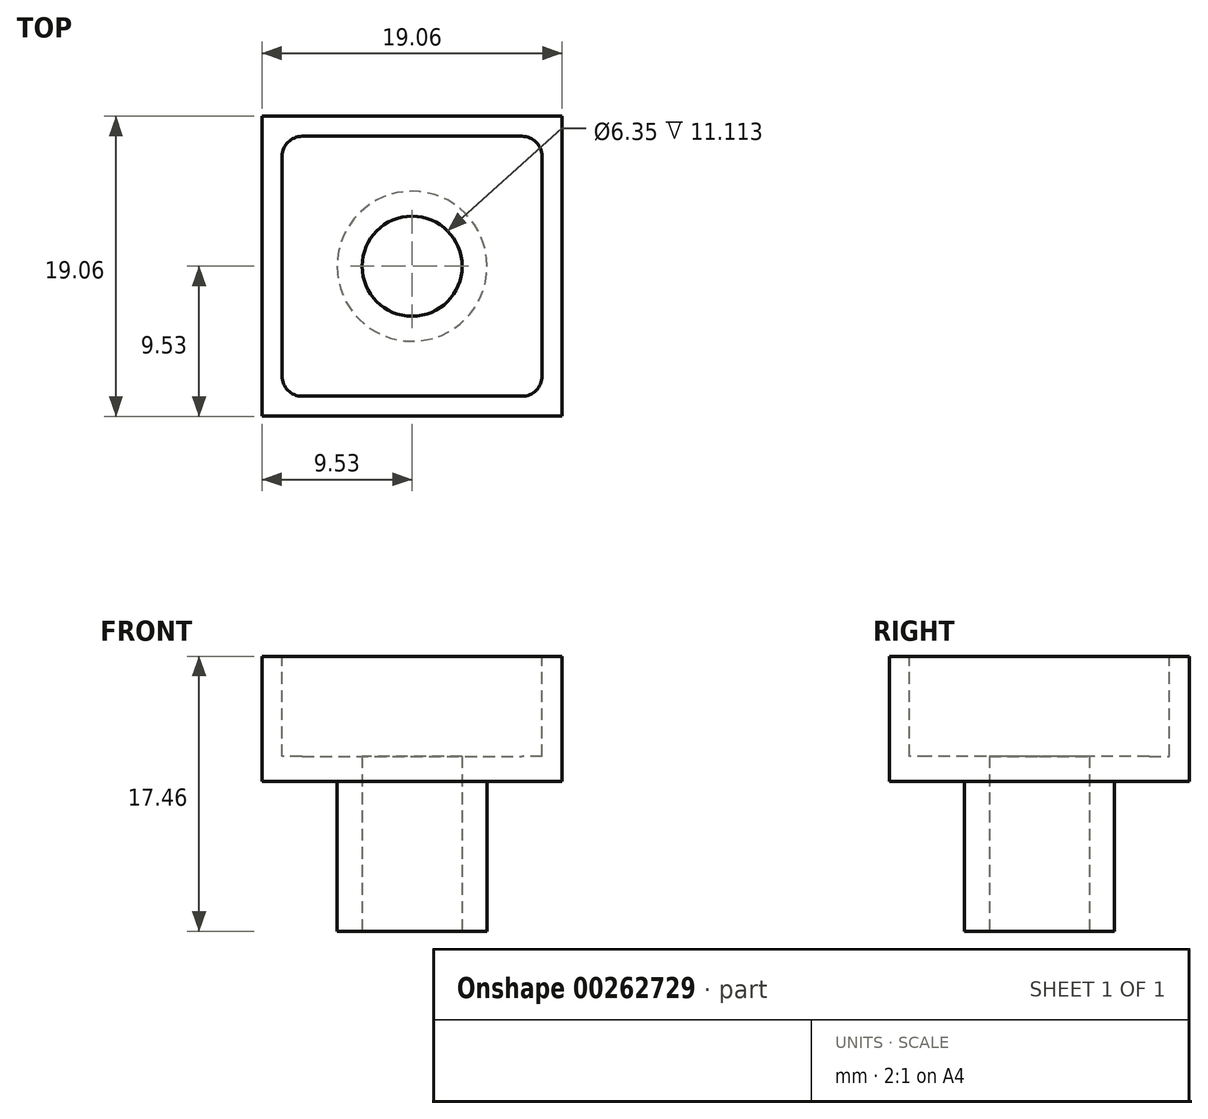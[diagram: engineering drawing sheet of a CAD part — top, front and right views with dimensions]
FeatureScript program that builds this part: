
annotation { "Feature Type Name" : "Feature", "Feature Type Description" : "" }
export const myFeature = defineFeature(function(context is Context, id is Id, definition is map)
    precondition{}
    {
        {
            var Q0;
            Q0=qCreatedBy(makeId("Top.planeOp"),FACE);
            var sketch = newSketch(context, id + "F0", { "sketchPlane" : qUnion([Q0])});
            skCircle(sketch, "E0", {"center": v(0, 0) * mm, "radius": 4.76 * mm});
            skSolve(sketch);
        }
        {
            var Q0;
            Q0 = qSketchRegion(id + "F0", true);
            extrude(context, id + "F1", {"entities" : qUnion([Q0]), "depth" : 17.46 * mm});
        }
        {
            var Q0;
            Q0=makeQuery(id+"F0.imprint","IMPRINT",FACE,{"disambiguationData":[TD([[makeQuery(id+"F0.imprint","IMPRINT",EDGE,{"derivedFrom":sQuery(id+"F0.wireOp",EDGE,"E0")}),1.0]])]});
            var sketch = newSketch(context, id + "F2", { "sketchPlane" : qUnion([Q0])});
            skCircle(sketch, "E1", {"center": v(0, 0) * mm, "radius": 3.18 * mm});
            skSolve(sketch);
        }
        {
            var Q0;
            Q0=qCreatedBy(makeId("Front.planeOp"),FACE);
            var sketch = newSketch(context, id + "F3", { "sketchPlane" : qUnion([Q0])});
            skLineSegment(sketch, "E2", {"start": v(0, 0) * mm, "end": v(0, 17.46) * mm, "construction": true});
            skLineSegment(sketch, "E3", {"start": v(0, 0) * mm, "end": v(-9.53, 0) * mm, "construction": true});
            skLineSegment(sketch, "E4.bottom", {"start": v(-9.52, 17.46) * mm, "end": v(9.52, 17.46) * mm});
            skLineSegment(sketch, "E4.top", {"start": v(-9.53, 9.53) * mm, "end": v(9.52, 9.53) * mm});
            skLineSegment(sketch, "E4.left", {"start": v(-9.53, 17.46) * mm, "end": v(-9.53, 9.53) * mm});
            skLineSegment(sketch, "E4.right", {"start": v(9.52, 17.46) * mm, "end": v(9.52, 9.53) * mm});
            skSolve(sketch);
        }
        {
            var Q0;
            Q0 = qSketchRegion(id + "F3", true);
            extrude(context, id + "F4", {"entities" : qUnion([Q0]), "operationType" : NewBodyOperationType.ADD, "endBound" : BoundingType.SYMMETRIC, "depth" : 19.05 * mm});
        }
        {
            var Q0;
            Q0=makeQuery(id+"F4.boolean.opBoolean","MERGE",FACE,{"derivedFrom":[makeQuery(id+"F1.opExtrude","CAP_FACE",FACE,{"disambiguationData":[OSD([sQuery(id+"F0.wireOp",EDGE,"E0")])],"isStart":false}),makeQuery(id+"F4.opExtrude","SWEPT_FACE",FACE,{"disambiguationData":[OSD([sQuery(id+"F3.wireOp",EDGE,"E4.bottom")])]})]});
            var sketch = newSketch(context, id + "F5", { "sketchPlane" : qUnion([Q0])});
            skLineSegment(sketch, "E5.bottom", {"start": v(-6.98, 8.26) * mm, "end": v(6.99, 8.26) * mm});
            skLineSegment(sketch, "E5.top", {"start": v(-6.98, -8.26) * mm, "end": v(6.99, -8.26) * mm});
            skLineSegment(sketch, "E5.left", {"start": v(-8.25, 6.99) * mm, "end": v(-8.25, -6.99) * mm});
            skLineSegment(sketch, "E5.right", {"start": v(8.26, 6.99) * mm, "end": v(8.26, -6.99) * mm});
            skPoint(sketch, "E6.visualSharp", {"position": v(-8.25, 8.26) * mm});
            skArc(sketch, "E6.filletArc", {"start": v(-6.98, 8.26) * mm, "mid": v(-7.88, 7.88) * mm, "end": v(-8.25, 6.99) * mm});
            skPoint(sketch, "E7.visualSharp", {"position": v(8.26, 8.26) * mm});
            skArc(sketch, "E7.filletArc", {"start": v(8.26, 6.99) * mm, "mid": v(7.88, 7.88) * mm, "end": v(6.99, 8.26) * mm});
            skPoint(sketch, "E8.visualSharp", {"position": v(8.26, -8.26) * mm});
            skArc(sketch, "E8.filletArc", {"start": v(6.99, -8.26) * mm, "mid": v(7.88, -7.88) * mm, "end": v(8.26, -6.99) * mm});
            skPoint(sketch, "E9.visualSharp", {"position": v(-8.25, -8.26) * mm});
            skArc(sketch, "E9.filletArc", {"start": v(-8.25, -6.99) * mm, "mid": v(-7.88, -7.88) * mm, "end": v(-6.98, -8.26) * mm});
            skSolve(sketch);
        }
        {
            var Q0;
            Q0 = qSketchRegion(id + "F5", true);
            extrude(context, id + "F6", {"entities" : qUnion([Q0]), "operationType" : NewBodyOperationType.REMOVE, "oppositeDirection" : true, "depth" : 6.35 * mm});
        }
        {
            var Q0;
            Q0 = qSketchRegion(id + "F2", true);
            extrude(context, id + "F7", {"entities" : qUnion([Q0]), "operationType" : NewBodyOperationType.REMOVE, "depth" : 17.46 * mm});
        }
    });
